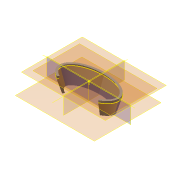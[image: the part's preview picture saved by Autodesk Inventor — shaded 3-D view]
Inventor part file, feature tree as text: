
AUTODESK INVENTOR PART (.ipt)
format: ipt  version: 2015 SP2 (Build 190223200, 223)  size: 378,368 bytes
history: native  units: mm
features: sketch x4, other x3, plane x2, loft x2
ambient origin geometry x8: Origin, YZ Plane, XZ Plane, XY Plane, X Axis, Y Axis, Z Axis, Center Point
bodies: Body1 (feature_tree)
feature tree (11):
  other  "Sólido1"
  sketch  "Boceto1"  dims[d0=26.4mm d1=13.3mm]
  plane  "Plano de trabajo1"
  plane  "Plano de trabajo2"
  loft  "Solevación1"
  sketch  "Boceto3"  dims[d4=2.0mm]
  loft  "Solevación2"
  sketch  "Boceto2"  dims[d2=26.4mm d3=13.3mm]
  sketch  "Boceto4"  dims[d5=-15.0mm d6=-2.0mm d8=1.0mm d9=0.0mm d10=90.0deg d11=0.0mm d12=90.0deg d13=2.0mm d15=4.0mm d16=0.0mm d17=90.0deg d18=0.0mm d19=90.0deg]
  other  "Aristas1"
  other  "Proyectar aristas de corte1"
